# Revit family: BasinMixer-Vitra-OriginSeries-A42556
name_source: partatom
category: Plumbing Fixtures
revit_build: Autodesk Revit 2017 (Build: 20160225_1515(x64)
units: mm (PartAtom-declared; Revit-internal decimal feet)

## family parameters
Cut with Voids When Loaded = No
Host = Face
OmniClass Number = 23.45.55.17
OmniClass Title = Mixing Faucets
Part Type = Normal
Room Calculation Point = No
Round Connector Dimension = Use Diameter
Shared = Yes

## types (14) — shared parameters
BIMobject category = Taps & Mixers
Brand = VitrA
CW Connection = Yes
Default Elevation = 850 mm  [stored 2.78871 ft]
Description = Origin single lever basin mixer - without waste set
Design country = Turkey
Flow Rate(L/min. - 3 bar) = 5L/min.
HW Connection = Yes
Hot Water Supply (max.) = 80 °C
Hot Water temperature, factory set to = 38 °C
IFC Classification = Sanitary Terminal
Main Material = Brass
Manufacturer = Vitra
Manufacturer name = Vitra
Masterformat 2014 Code = 22 40 00
Masterformat 2014 Description = Plumbing Fixtures
Min. flow pressure of = 0.5 bar
Mounting type = Countertop
NBS Referans Code = 45-35-70/371
NBS Referans Description = Water supply fittings for wash basins and troughs
Nominal Depth (mm) = 170 mm  [stored 0.557743 ft]
Nominal Height (mm) = 215 mm  [stored 0.705381 ft]
Nominal Width (mm) = 60 mm  [stored 0.19685 ft]
Number Of Connections = 2
OmniClass Code = 23.45.55.17
OmniClass Description = Mixing Faucets
Product Properties = Extra Water Saving, Green Building Certification, Energy Saving, Easy İnstallation
Product Type = Basin Mixer
Product certification = https://www.vitraglobal.com
Product family = Origin
Product group = Origin Basin Mixer
Range of Hot Water Supply = 5 - 65 °C
Range of flow pressure = 1 - 5 bar
Test Pressure = 16 bar
URL = https://vitraglobal.com
Uniclass 1.4 Code = L725111
Uniclass 1.4 Description = Mixer taps
Uniclass 2.0 Code = Pr_40_30_96_98
Uniclass 2.0 Description = Washbasin Tap
Uniclass 2015 Code = Pr_40_20_87_98
Uniclass 2015 Name = Washbasin Tap
Uniformat II Code = 22 40 00
Uniformat II Description = Plumbing Fixture
Vent Connection = No
Warranty Period (Year) = 10 Years
Waste Connection = No
Weight Net (kg) = 2
Youtube = https://www.youtube.com

## per-type parameters (varying)
| type | Article No. (default) | Coating Material | Color | Connection Diameter (mm) | Installation instructions | Model | Product Guid | Product SKU | Product url | Technical description |
| BasinMixer-Vitra-OriginSeries(MatteBlack)-A4255636 | A4255636 | Matte Black | Matte Black | 10 mm  [stored 0.0328084 ft] | file://ygbzfilesrv/ArtemaBarcod/Attach/A79558.pdf | A4255636 | file://ygbzfilesrv/ArtemaBarcod/Attach/A79491.pdf | A4255636 | https://www.vitra.com.tr | https://www.vitra.com.tr |
| BasinMixer-Vitra-OriginSeries(Nickel)-A4255634 | A4255634 | Nickel | Nickel | 10 mm  [stored 0.0328084 ft] | file://ygbzfilesrv/ArtemaBarcod/Attach/A79558.pdf | A4255634 | file://ygbzfilesrv/ArtemaBarcod/Attach/A79491.pdf | A4255634 | https://www.vitra.com.tr | https://www.vitra.com.tr |
| BasinMixer-Vitra-OriginSeries(BrightCopper)-A4255626 | A4255626 | BrightCopper | Bright Copper | 10 mm  [stored 0.0328084 ft] | file://ygbzfilesrv/ArtemaBarcod/Attach/A79558.pdf | A4255626 | file://ygbzfilesrv/ArtemaBarcod/Attach/A79491.pdf | A4255626 | https://www.vitra.com.tr | https://www.vitra.com.tr |
| BasinMixer-Vitra-OriginSeries(Chrome)-A42556 | A42556 | Chrome | Chrome | 10 mm  [stored 0.0328084 ft] | file://ygbzfilesrv/ArtemaBarcod/Attach/A79558.pdf | A42556 | file://ygbzfilesrv/ArtemaBarcod/Attach/A79491.pdf | A42556 | https://www.vitra.com.tr | https://www.vitra.com.tr |
| BasinMixer-Vitra-OriginSeries(BrightCopper)-A4255626EXP | A4255626EXP | BrightCopper | Bright Copper | 10 mm  [stored 0.0328084 ft] |  | A4255626EXP |  | A4255626EXP | https://www.vitraglobal.com | https://www.vitraglobal.com |
| BasinMixer-Vitra-OriginSeries(BrightCopper)-A4255626IND | A4255626EXP | BrightCopper | Bright Copper | 10 mm  [stored 0.0328084 ft] |  | A4255626IND |  | A4255626EXP | https://www.vitra-india.com | https://www.vitra-india.com |
| BasinMixer-Vitra-OriginSeries(BrightCopper)-A4255626VUK | A4255626VUK | BrightCopper | Bright Copper | 15 mm  [stored 0.0492126 ft] |  | A4255626VUK |  | A4255626VUK | https://www.vitra.co.uk | https://www.vitra.co.uk |
| BasinMixer-Vitra-OriginSeries(Nickel)-A4255634IND | A4255634IND | Nickel | Brushed Nickel | 15 mm  [stored 0.0492126 ft] |  | A4255634IND |  | A4255634IND | https://www.vitra-india.com | https://www.vitra-india.com |
| BasinMixer-Vitra-OriginSeries(Nickel)-A4255634VUK | A4255634VUK | Nickel | Brushed Nickel | 15 mm  [stored 0.0492126 ft] |  | A4255634VUK |  | A4255634VUK | https://www.vitra.co.uk | https://www.vitra.co.uk |
| BasinMixer-Vitra-OriginSeries(MatteBlack)-A4255636IND | A4255636IND | Matte Black | Matte Black | 15 mm  [stored 0.0492126 ft] |  | A4255636IND |  | A4255636IND | https://www.vitra-india.com | https://www.vitra-india.com |
| BasinMixer-Vitra-OriginSeries(MatteBlack)-A4255636VUK | A4255636VUK | Matte Black | Matte Black | 15 mm  [stored 0.0492126 ft] |  | A4255636VUK |  | A4255636VUK | https://www.vitra.co.uk | https://www.vitra.co.uk |
| BasinMixer-Vitra-OriginSeries(Chrome)-A42556EXP | A42556EXP | Chrome | Chrome | 10 mm  [stored 0.0328084 ft] |  | A42556EXP |  | A42556EXP | https://www.vitraglobal.com | https://www.vitraglobal.com |
| BasinMixer-Vitra-OriginSeries(Chrome)-A42556IND | A42556IND | Chrome | Chrome | 15 mm  [stored 0.0492126 ft] |  | A42556IND |  | A42556IND | https://www.vitra-india.com | https://www.vitra-india.com |
| BasinMixer-Vitra-OriginSeries(Chrome)-A42556VUK | A42556VUK | Chrome | Chrome | 15 mm  [stored 0.0492126 ft] |  | A42556VUK |  | A42556VUK | https://www.vitra.co.uk | https://www.vitra.co.uk |

note: [stored X ft] marks values corroborated as IEEE doubles in the binary element streams (Revit-internal decimal feet)

## geometry (parser evidence)
native form markers: Sweep x1
no freeform markers — native parametric forms only
